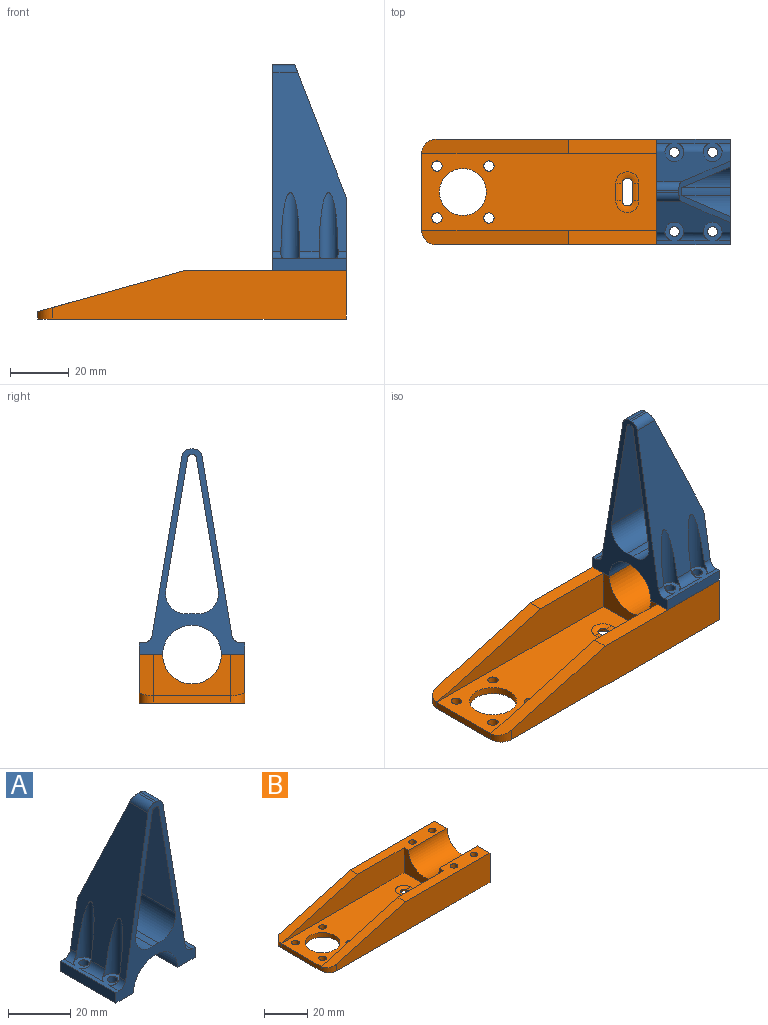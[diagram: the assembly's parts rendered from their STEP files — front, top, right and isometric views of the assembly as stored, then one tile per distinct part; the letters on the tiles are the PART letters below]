
ASSEMBLY  parts=2 mates=1
PART A: 37 faces, bbox 36x25x70 mm
  f0: cylinder r=3mm len=8.48mm, axis (0,-1,0), area 33.1mm2, adj f1,f11,f12,f36
  f1: plane 60.99x25mm, normal (-0.99,0,0.16), area 981.4mm2, adj f0,f10,f11,f23,f25,f26,f27,f28
  f2: cylinder r=3mm len=8.48mm, axis (0,-1,0), area 33.1mm2, adj f3,f11,f12,f36
  f3: plane 60.99x25mm, normal (0.99,0,0.16), area 981.4mm2, adj f2,f10,f11,f18,f20,f29,f30,f31
  f4: plane 8.28x0.92mm, normal (0,0,-1), area 7.6mm2, adj f5,f8,f11,f36
  f5: cylinder r=1mm len=8.6mm, axis (0,-1,0), area 11.8mm2, adj f4,f6,f11,f36
  f6: plane 45.12x25mm, normal (0.99,0,-0.16), area 793mm2, adj f5,f10,f11,f32,f36
  f7: plane 45.12x25mm, normal (-0.99,0,-0.16), area 793mm2, adj f8,f10,f11,f34,f36
  f8: cylinder r=1mm len=8.6mm, axis (0,-1,0), area 11.8mm2, adj f4,f7,f11,f36
  f9: plane 25x8mm, normal (0,0,-1), area 181.8mm2, adj f10,f11,f13,f16,f19,f35
  f10: plane 36x25mm, normal (0,1,0), area 326.2mm2, adj f1,f3,f6,f7,f9,f13,f14,f15
  f11: plane 70x36mm, normal (0,-1,0), area 511mm2, adj f0,f1,f2,f3,f4,f5,f6,f7
  f12: plane 7.5x0.92mm, normal (0,0,1), area 6.9mm2, adj f0,f2,f11,f36
  f13: plane 25x4mm, normal (1,0,0), area 100mm2, adj f9,f10,f11,f17
  f14: plane 25x4mm, normal (-1,0,0), area 100mm2, adj f10,f11,f15,f22
  f15: plane 25x8mm, normal (0,0,-1), area 181.8mm2, adj f10,f11,f14,f21,f24,f35
  f16: cylinder r=1.7mm len=4mm, axis (0,0,1), area 42.7mm2, adj f9,f17
  f17: plane 25x7.75mm, normal (0,0,1), area 84mm2, adj f10,f11,f13,f16,f18,f19,f20,f29
  f18: cylinder r=3.25mm len=22.57mm, axis (0,0,1), area 161.7mm2, adj f3,f17,f30,f31
  f19: cylinder r=1.7mm len=4mm, axis (0,0,1), area 42.7mm2, adj f9,f17
  f20: cylinder r=3.25mm len=22.57mm, axis (0,0,1), area 161.7mm2, adj f3,f17,f29,f31
  f21: cylinder r=1.7mm len=4mm, axis (0,0,1), area 42.7mm2, adj f15,f22
  f22: plane 25x7.75mm, normal (0,0,1), area 84mm2, adj f10,f11,f14,f21,f23,f24,f25,f26
  f23: cylinder r=3.25mm len=22.57mm, axis (0,0,1), area 161.7mm2, adj f1,f22,f26,f27
  f24: cylinder r=1.7mm len=4mm, axis (0,0,1), area 42.7mm2, adj f15,f22
  f25: cylinder r=3.25mm len=22.57mm, axis (0,0,1), area 161.7mm2, adj f1,f22,f27,f28
  f26: cylinder r=3mm len=4.85mm, axis (0,-1,0), area 13.5mm2, adj f1,f10,f22,f23
  f27: cylinder r=3mm len=10.71mm, axis (0,-1,0), area 31.1mm2, adj f1,f22,f23,f25
  f28: cylinder r=3mm len=4.85mm, axis (0,-1,0), area 13.5mm2, adj f1,f11,f22,f25
  f29: cylinder r=3mm len=4.85mm, axis (0,-1,0), area 13.5mm2, adj f3,f10,f17,f20
  f30: cylinder r=3mm len=4.85mm, axis (0,-1,0), area 13.5mm2, adj f3,f11,f17,f18
  f31: cylinder r=3mm len=10.71mm, axis (0,-1,0), area 31.1mm2, adj f3,f17,f18,f20
  f32: cylinder r=7mm len=25mm, axis (0,-1,0), area 321mm2, adj f6,f10,f11,f33
  f33: cylinder r=14mm len=25mm, axis (0,-1,0), area 68.8mm2, adj f10,f11,f32,f34
  f34: cylinder r=7mm len=25mm, axis (0,-1,0), area 321mm2, adj f7,f10,f11,f33
  f35: cylinder r=10mm len=25mm, axis (0,-1,0), area 785.4mm2, adj f9,f10,f11,f15
  f36: plane 45x21mm, normal (0,0.93,0.36), area 198.2mm2, adj f0,f1,f2,f3,f4,f5,f6,f7
PART B: 61 faces, bbox 105x36x16.5 mm
  f0: plane 105x36mm, normal (0,0,-1), area 3315.8mm2, adj f6,f9,f11,f14,f15,f16,f17,f18
  f1: cylinder r=1.7mm len=11.5mm, axis (0,0,-1), area 122.8mm2, adj f10,f60
  f2: cylinder r=1.7mm len=11.5mm, axis (0,0,-1), area 122.8mm2, adj f5,f53
  f3: cylinder r=1.7mm len=11.5mm, axis (0,0,-1), area 122.8mm2, adj f5,f46
  f4: cylinder r=1.7mm len=11.5mm, axis (0,0,-1), area 122.8mm2, adj f10,f39
  f5: plane 55x8mm, normal (0,0,1), area 331.8mm2, adj f2,f3,f6,f7,f11,f13,f20,f22
  f6: plane 36x16.5mm, normal (1,0,0), area 436.9mm2, adj f0,f5,f9,f10,f11,f22
  f7: plane 26x14mm, normal (-1,0,0), area 206.9mm2, adj f5,f8,f10,f12,f13,f22
  f8: plane 80x26mm, normal (0,0,1), area 1744.8mm2, adj f7,f12,f13,f14,f15,f16,f17,f18
  f9: plane 100x16.5mm, normal (0,-1,0), area 1366.5mm2, adj f0,f6,f10,f21,f24
  f10: plane 55x8mm, normal (0,0,1), area 331.8mm2, adj f1,f4,f6,f7,f9,f12,f21,f22
  f11: plane 100x16.5mm, normal (0,1,0), area 1366.5mm2, adj f0,f5,f6,f20,f23
  f12: plane 80x14mm, normal (0,1,0), area 770mm2, adj f7,f8,f10,f21
  f13: plane 80x14mm, normal (0,-1,0), area 770mm2, adj f5,f7,f8,f20
  f14: plane 26x2.5mm, normal (-1,0,0), area 65mm2, adj f0,f8,f23,f24
  f15: cylinder r=1.75mm len=3.5mm, axis (0,0,-1), area 27.5mm2, adj f0,f8
  f16: cylinder r=8mm len=16mm, axis (0,0,-1), area 125.7mm2, adj f0,f8
  f17: cylinder r=1.75mm len=3.5mm, axis (0,0,-1), area 27.5mm2, adj f0,f8
  f18: cylinder r=1.75mm len=3.5mm, axis (0,0,-1), area 27.5mm2, adj f0,f8
  f19: cylinder r=1.75mm len=3.5mm, axis (0,0,-1), area 27.5mm2, adj f0,f8
  f20: plane 50x14mm, normal (-0.27,0,0.96), area 254mm2, adj f5,f11,f13,f23
  f21: plane 50x14mm, normal (-0.27,0,0.96), area 254mm2, adj f9,f10,f12,f24
  f22: cylinder r=10mm len=25mm, axis (1,0,0), area 785.4mm2, adj f5,f6,f7,f10
  f23: cylinder r=5mm len=5mm, axis (0,0,1), area 23.6mm2, adj f0,f11,f14,f20
  f24: cylinder r=5mm len=5mm, axis (0,0,-1), area 23.6mm2, adj f0,f9,f14,f21
  f25: cylinder r=2mm len=6mm, axis (0,1,0), area 18.8mm2, adj f0,f26,f27,f29
  f26: torus R=3.75mm, axis (0,0,1), area 24.4mm2, adj f0,f25,f28,f30
  f27: torus R=3.75mm, axis (0,0,1), area 24.4mm2, adj f0,f25,f28,f31
  f28: cylinder r=2mm len=6mm, axis (0,-1,0), area 18.8mm2, adj f0,f26,f27,f32
  f29: cylinder r=5mm len=6mm, axis (0,-1,0), area 13.5mm2, adj f8,f25,f30,f31
  f30: torus R=3.93mm, axis (0,0,1), area 20mm2, adj f8,f26,f29,f32
  f31: torus R=3.93mm, axis (0,0,1), area 20mm2, adj f8,f27,f29,f32
  f32: cylinder r=5mm len=6mm, axis (0,-1,0), area 13.5mm2, adj f8,f28,f30,f31
  f33: plane 5x3mm, normal (-0.87,-0.5,0), area 17.3mm2, adj f0,f34,f38,f39
  f34: plane 5x3mm, normal (-0.87,0.5,0), area 17.3mm2, adj f0,f33,f35,f39
  f35: plane 5x3.46mm, normal (0,1,0), area 17.3mm2, adj f0,f34,f36,f39
  f36: plane 5x3mm, normal (0.87,0.5,0), area 17.3mm2, adj f0,f35,f37,f39
  f37: plane 5x3mm, normal (0.87,-0.5,0), area 17.3mm2, adj f0,f36,f38,f39
  f38: plane 5x3.46mm, normal (0,-1,0), area 17.3mm2, adj f0,f33,f37,f39
  f39: plane 6.93x6mm, normal (0,0,-1), area 22.1mm2, adj f4,f33,f34,f35,f36,f37,f38
  f40: plane 5x3mm, normal (-0.87,-0.5,0), area 17.3mm2, adj f0,f41,f45,f46
  f41: plane 5x3mm, normal (-0.87,0.5,0), area 17.3mm2, adj f0,f40,f42,f46
  f42: plane 5x3.46mm, normal (0,1,0), area 17.3mm2, adj f0,f41,f43,f46
  f43: plane 5x3mm, normal (0.87,0.5,0), area 17.3mm2, adj f0,f42,f44,f46
  f44: plane 5x3mm, normal (0.87,-0.5,0), area 17.3mm2, adj f0,f43,f45,f46
  f45: plane 5x3.46mm, normal (0,-1,0), area 17.3mm2, adj f0,f40,f44,f46
  f46: plane 6.93x6mm, normal (0,0,-1), area 22.1mm2, adj f3,f40,f41,f42,f43,f44,f45
  f47: plane 5x3mm, normal (-0.87,-0.5,0), area 17.3mm2, adj f0,f48,f52,f53
  f48: plane 5x3mm, normal (-0.87,0.5,0), area 17.3mm2, adj f0,f47,f49,f53
  f49: plane 5x3.46mm, normal (0,1,0), area 17.3mm2, adj f0,f48,f50,f53
  f50: plane 5x3mm, normal (0.87,0.5,0), area 17.3mm2, adj f0,f49,f51,f53
  f51: plane 5x3mm, normal (0.87,-0.5,0), area 17.3mm2, adj f0,f50,f52,f53
  f52: plane 5x3.46mm, normal (0,-1,0), area 17.3mm2, adj f0,f47,f51,f53
  f53: plane 6.93x6mm, normal (0,0,-1), area 22.1mm2, adj f2,f47,f48,f49,f50,f51,f52
  f54: plane 5x3mm, normal (-0.87,-0.5,0), area 17.3mm2, adj f0,f55,f59,f60
  f55: plane 5x3mm, normal (-0.87,0.5,0), area 17.3mm2, adj f0,f54,f56,f60
  f56: plane 5x3.46mm, normal (0,1,0), area 17.3mm2, adj f0,f55,f57,f60
  f57: plane 5x3mm, normal (0.87,0.5,0), area 17.3mm2, adj f0,f56,f58,f60
  f58: plane 5x3mm, normal (0.87,-0.5,0), area 17.3mm2, adj f0,f57,f59,f60
  f59: plane 5x3.46mm, normal (0,-1,0), area 17.3mm2, adj f0,f54,f58,f60
  f60: plane 6.93x6mm, normal (0,0,-1), area 22.1mm2, adj f1,f54,f55,f56,f57,f58,f59
PLACE A rot(axis=(0,0,-1),90deg) t=(38.27,4.55,12.91)mm
PLACE B t=(50.77,-13.45,-3.59)mm
MATE fastened A.f16 <-> B.f4  axis (0,0,-1) through (31.77,-8.95,12.91)mm
